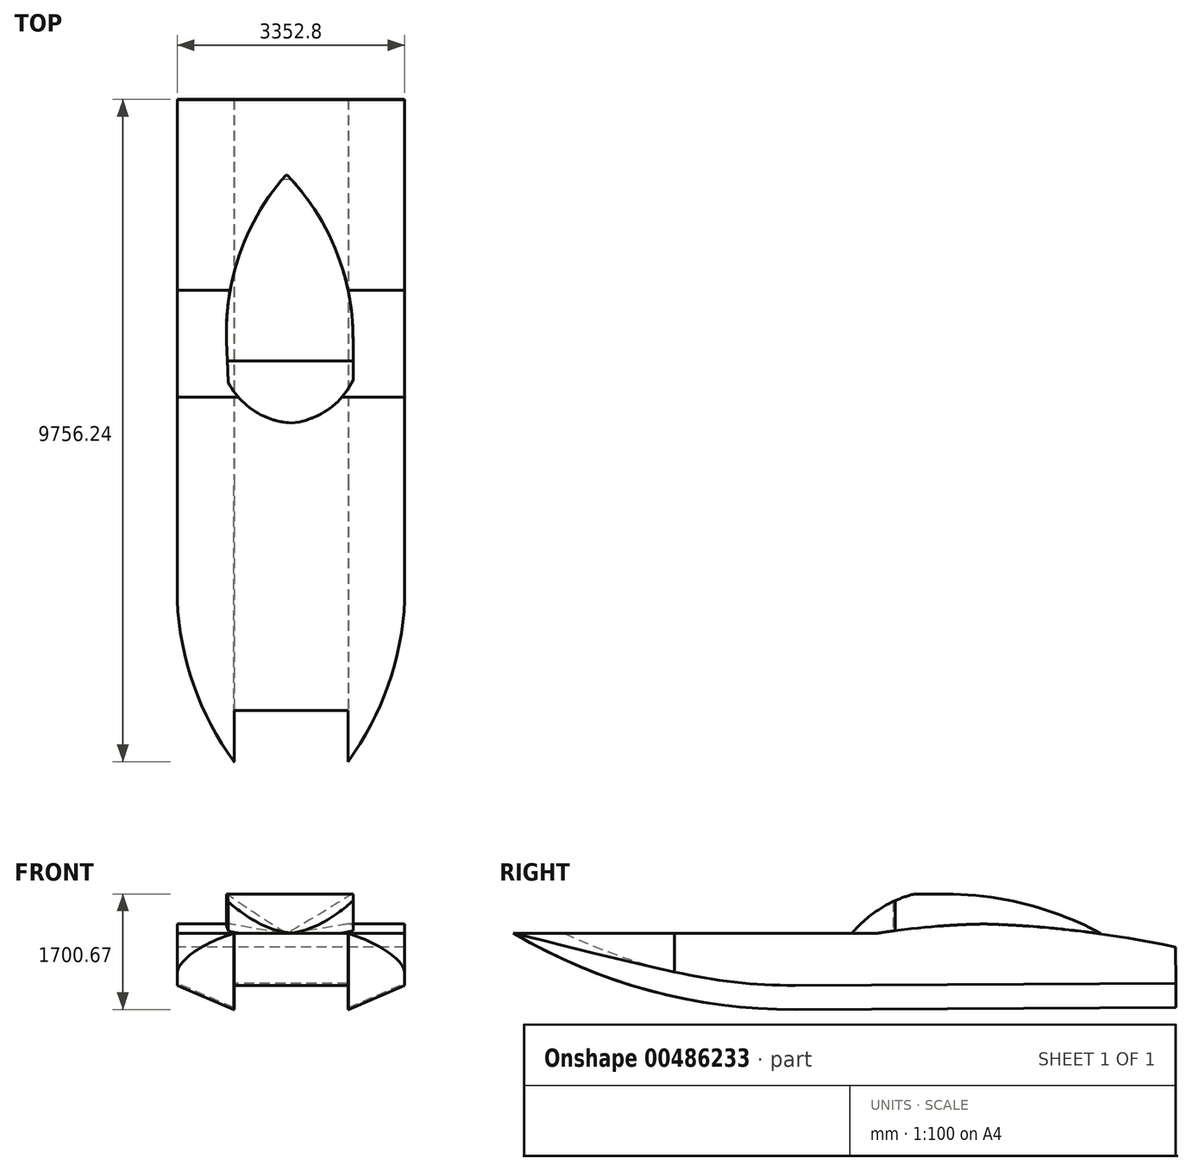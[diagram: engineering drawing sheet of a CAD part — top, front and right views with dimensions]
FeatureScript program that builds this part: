
annotation { "Feature Type Name" : "Feature", "Feature Type Description" : "" }
export const myFeature = defineFeature(function(context is Context, id is Id, definition is map)
    precondition{}
    {
        {
            var Q0;
            Q0=qCreatedBy(makeId("Right.planeOp"),FACE);
            var sketch = newSketch(context, id + "F0", { "sketchPlane" : qUnion([Q0])});
            skLineSegment(sketch, "E0", {"start": v(9903.4, 2819.64) * mm, "end": v(9906.18, 2286.25) * mm});
            skLineSegment(sketch, "E1", {"start": v(9906.18, 2286.25) * mm, "end": v(4296.5, 2257.1) * mm});
            skLineSegment(sketch, "E2", {"start": v(7101.34, 2271.67) * mm, "end": v(7096.72, 3160.66) * mm, "construction": true});
            skArc(sketch, "E3", {"start": v(9903.4, 2819.64) * mm, "mid": v(8507.76, 3053.5) * mm, "end": v(7096.72, 3160.66) * mm});
            skLineSegment(sketch, "E4", {"start": v(5524.18, 2263.47) * mm, "end": v(5520.22, 3025.46) * mm, "construction": true});
            skArc(sketch, "E5", {"start": v(7096.72, 3160.66) * mm, "mid": v(6306.11, 3120.55) * mm, "end": v(5520.22, 3025.46) * mm});
            skLineSegment(sketch, "E6", {"start": v(5520.22, 3025.46) * mm, "end": v(149.94, 3025.46) * mm});
            skArc(sketch, "E7", {"start": v(149.94, 3025.46) * mm, "mid": v(2186.92, 2445.37) * mm, "end": v(4296.5, 2257.1) * mm});
            skLineSegment(sketch, "E8", {"start": v(4296.5, 2257.1) * mm, "end": v(4298.35, 1901.5) * mm, "construction": true});
            skLineSegment(sketch, "E9", {"start": v(4298.35, 1901.5) * mm, "end": v(9906.18, 1930.65) * mm});
            skLineSegment(sketch, "E10", {"start": v(9906.18, 1930.65) * mm, "end": v(9906.18, 2286.25) * mm});
            skArc(sketch, "E11", {"start": v(149.94, 3025.46) * mm, "mid": v(2147.87, 2181.98) * mm, "end": v(4298.35, 1901.5) * mm});
            skSolve(sketch);
        }
        {
            var Q0;
            Q0=qSketchRegion(id+"F0",true);
            extrude(context, id + "F1", {"entities" : qUnion([Q0]), "depth" : 3352.8 * mm, "offsetDistance" : 25.4 * mm});
        }
        {
            var Q0;
            Q0=makeQuery(id+"F1.opExtrude","SWEPT_FACE",FACE,{"disambiguationData":[OSD([sQuery(id+"F0.wireOp",EDGE,"E6")])]});
            var sketch = newSketch(context, id + "F2", { "sketchPlane" : qUnion([Q0])});
            skLineSegment(sketch, "E12", {"start": v(1676.4, 5520.22) * mm, "end": v(1676.4, 5139.22) * mm, "construction": true});
            skLineSegment(sketch, "E13", {"start": v(1676.4, 5520.22) * mm, "end": v(2590.8, 5520.22) * mm, "construction": true});
            skLineSegment(sketch, "E14", {"start": v(2590.8, 5520.22) * mm, "end": v(1676.4, 5520.22) * mm, "construction": true});
            skLineSegment(sketch, "E15", {"start": v(1676.4, 5520.22) * mm, "end": v(762, 5520.22) * mm, "construction": true});
            skLineSegment(sketch, "E16", {"start": v(1612.43, 8801.7) * mm, "end": v(1676.4, 5520.22) * mm, "construction": true});
            skLineSegment(sketch, "E17", {"start": v(2590.8, 5520.22) * mm, "end": v(2590.8, 5774.22) * mm, "construction": true});
            skLineSegment(sketch, "E18", {"start": v(2590.8, 5774.22) * mm, "end": v(2590.8, 6383.82) * mm});
            skArc(sketch, "E19", {"start": v(1676.4, 5139.22) * mm, "mid": v(2218.54, 5334.4) * mm, "end": v(2590.8, 5774.22) * mm});
            skArc(sketch, "E20.MirrorCS", {"start": v(1691.25, 5139.5) * mm, "mid": v(1141.92, 5313.42) * mm, "end": v(752.8, 5738.38) * mm});
            skLineSegment(sketch, "E21.MirrorCS", {"start": v(752.8, 5738.38) * mm, "end": v(729.04, 6347.52) * mm});
            skArc(sketch, "E22", {"start": v(1612.43, 8801.7) * mm, "mid": v(931.87, 7660.59) * mm, "end": v(729.04, 6347.52) * mm});
            skArc(sketch, "E23", {"start": v(2590.8, 6383.82) * mm, "mid": v(2336.94, 7687.98) * mm, "end": v(1612.43, 8801.7) * mm});
            skLineSegment(sketch, "E24", {"start": v(2590.8, 6383.82) * mm, "end": v(2590.8, 5774.22) * mm});
            skSolve(sketch);
        }
        {
            var Q0;
            Q0=qSketchRegion(id+"F2",true);
            extrude(context, id + "F3", {"entities" : qUnion([Q0]), "operationType" : NewBodyOperationType.ADD, "depth" : 914.4 * mm, "offsetDistance" : 25.4 * mm});
        }
        {
            var Q0;
            Q0=makeQuery(id+"F1.opExtrude","CAP_FACE",FACE,{"disambiguationData":[OSD([sQuery(id+"F0.wireOp",EDGE,"E0"),sQuery(id+"F0.wireOp",EDGE,"E1"),sQuery(id+"F0.wireOp",EDGE,"E3"),sQuery(id+"F0.wireOp",EDGE,"E5"),sQuery(id+"F0.wireOp",EDGE,"E6"),sQuery(id+"F0.wireOp",EDGE,"E7")])],"isStart":false});
            var sketch = newSketch(context, id + "F4", { "sketchPlane" : qUnion([Q0])});
            skArc(sketch, "E25", {"start": v(6051.27, 3602.06) * mm, "mid": v(5549.4, 3384.98) * mm, "end": v(5137.42, 3025.46) * mm});
            skLineSegment(sketch, "E26", {"start": v(6051.27, 3602.06) * mm, "end": v(6508.47, 3602.06) * mm});
            skLineSegment(sketch, "E27", {"start": v(5137.42, 3025.46) * mm, "end": v(5137.42, 4052.91) * mm});
            skLineSegment(sketch, "E28", {"start": v(5137.42, 4052.91) * mm, "end": v(8976.57, 4052.91) * mm});
            skArc(sketch, "E29", {"start": v(8816.33, 3012.9) * mm, "mid": v(7699.4, 3452.45) * mm, "end": v(6508.47, 3602.06) * mm});
            skLineSegment(sketch, "E30", {"start": v(8816.33, 3012.9) * mm, "end": v(8976.57, 4052.91) * mm});
            skSolve(sketch);
        }
        {
            var Q0;
            Q0=qSketchRegion(id+"F4",true);
            extrude(context, id + "F5", {"entities" : qUnion([Q0]), "operationType" : NewBodyOperationType.REMOVE, "oppositeDirection" : true, "depth" : 3352.8 * mm, "offsetDistance" : 25.4 * mm});
        }
        {
            var Q0;
            Q0=makeQuery(id+"F1.opExtrude","SWEPT_FACE",FACE,{"disambiguationData":[OSD([sQuery(id+"F0.wireOp",EDGE,"E0")])]});
            var sketch = newSketch(context, id + "F6", { "sketchPlane" : qUnion([Q0])});
            skSolve(sketch);
        }
        {
            var Q0;
            Q0=makeQuery(id+"F1.opExtrude","SWEPT_FACE",FACE,{"disambiguationData":[OSD([sQuery(id+"F0.wireOp",EDGE,"E10")])]});
            var sketch = newSketch(context, id + "F7", { "sketchPlane" : qUnion([Q0])});
            skLineSegment(sketch, "E31", {"start": v(-1676.4, 2286.25) * mm, "end": v(0, 2286.25) * mm, "construction": true});
            skLineSegment(sketch, "E32", {"start": v(0, 2286.25) * mm, "end": v(-1676.4, 2286.25) * mm, "construction": true});
            skLineSegment(sketch, "E33", {"start": v(-1676.4, 2286.25) * mm, "end": v(-3352.8, 2286.25) * mm, "construction": true});
            skLineSegment(sketch, "E34", {"start": v(-1676.4, 2286.25) * mm, "end": v(-838.2, 2286.25) * mm, "construction": true});
            skLineSegment(sketch, "E35", {"start": v(-838.2, 2286.25) * mm, "end": v(-1676.4, 2286.25) * mm, "construction": true});
            skLineSegment(sketch, "E36", {"start": v(-1676.4, 2286.25) * mm, "end": v(-2514.6, 2286.25) * mm, "construction": true});
            skLineSegment(sketch, "E37", {"start": v(-2514.6, 2286.25) * mm, "end": v(-2514.6, 1930.65) * mm});
            skLineSegment(sketch, "E38", {"start": v(-838.2, 2286.25) * mm, "end": v(-838.2, 1930.65) * mm});
            skLineSegment(sketch, "E39", {"start": v(-3352.8, 1742.88) * mm, "end": v(-3352.8, 2286.25) * mm});
            skLineSegment(sketch, "E40", {"start": v(-2514.6, 1930.65) * mm, "end": v(-2514.6, 1742.88) * mm});
            skLineSegment(sketch, "E41", {"start": v(-2514.6, 1742.88) * mm, "end": v(-838.2, 1742.88) * mm});
            skLineSegment(sketch, "E42", {"start": v(-838.2, 1742.88) * mm, "end": v(-838.2, 1930.65) * mm});
            skLineSegment(sketch, "E43", {"start": v(0, 2286.25) * mm, "end": v(381.6, 2006.47) * mm});
            skLineSegment(sketch, "E44", {"start": v(-838.2, 1742.88) * mm, "end": v(192.5, 1742.88) * mm});
            skLineSegment(sketch, "E45", {"start": v(192.5, 1742.88) * mm, "end": v(381.6, 2006.47) * mm});
            skLineSegment(sketch, "E46", {"start": v(-3352.8, 1742.88) * mm, "end": v(-2514.6, 1742.88) * mm});
            skLineSegment(sketch, "E47", {"start": v(-838.2, 1930.65) * mm, "end": v(-831.85, 1930.65) * mm});
            skLineSegment(sketch, "E48", {"start": v(-831.85, 1930.65) * mm, "end": v(0, 2286.25) * mm});
            skLineSegment(sketch, "E49", {"start": v(-1676.4, 2286.25) * mm, "end": v(-1676.4, 1972.3) * mm, "construction": true});
            skLineSegment(sketch, "E50.MirrorCS", {"start": v(-2514.6, 1930.65) * mm, "end": v(-2520.95, 1930.65) * mm});
            skLineSegment(sketch, "E51.MirrorCS", {"start": v(-2520.95, 1930.65) * mm, "end": v(-3352.8, 2286.25) * mm});
            skSolve(sketch);
        }
        {
            var Q0;
            {var subQ0=sQuery(id+"F7.wireOp",EDGE,"E51.MirrorCS");Q0=makeQuery(id+"F7.imprint","IMPRINT",FACE,{"disambiguationData":[TD([[makeQuery(id+"F7.imprint","IMPRINT",EDGE,{"derivedFrom":subQ0}),1.0]])]});}
            var Q1;
            Q1=makeQuery(id+"F7.imprint","IMPRINT",FACE,{"disambiguationData":[TD([[makeQuery(id+"F7.imprint","IMPRINT",EDGE,{"derivedFrom":sQuery(id+"F7.wireOp",EDGE,"E40")}),-1.0]])]});
            var Q2;
            {var subQ0=sQuery(id+"F7.wireOp",EDGE,"E40");Q2=makeQuery(id+"F7.imprint","IMPRINT",FACE,{"disambiguationData":[TD([[makeQuery(id+"F7.imprint","IMPRINT",EDGE,{"derivedFrom":subQ0}),1.0]])]});}
            var Q3;
            Q3=makeQuery(id+"F7.imprint","IMPRINT",FACE,{"disambiguationData":[TD([[makeQuery(id+"F7.imprint","IMPRINT",EDGE,{"derivedFrom":sQuery(id+"F7.wireOp",EDGE,"E42")}),-1.0]])]});
            var Q4;
            {var subQ0=sQuery(id+"F7.wireOp",EDGE,"E48");Q4=makeQuery(id+"F7.imprint","IMPRINT",FACE,{"disambiguationData":[TD([[makeQuery(id+"F7.imprint","IMPRINT",EDGE,{"derivedFrom":subQ0}),-1.0]])]});}
            var Q5;
            {var subQ0=sQuery(id+"F7.wireOp",EDGE,"E37");Q5=makeQuery(id+"F7.imprint","IMPRINT",FACE,{"disambiguationData":[TD([[makeQuery(id+"F7.imprint","IMPRINT",EDGE,{"derivedFrom":subQ0}),1.0]])]});}
            var Q6;
            Q6=makeQuery(id+"F1.opExtrude","CAP_EDGE",EDGE,{"disambiguationData":[OSD([sQuery(id+"F0.wireOp",EDGE,"E9")])],"isStart":false});
            var Q7;
            Q7=makeQuery(id+"F1.opExtrude","CAP_EDGE",EDGE,{"disambiguationData":[OSD([sQuery(id+"F0.wireOp",EDGE,"E11")])],"isStart":false});
            sweep(context, id + "F8", {"operationType" : NewBodyOperationType.REMOVE, "profiles" : qUnion([Q0, Q1, Q2, Q3, Q4, Q5]), "path" : qUnion([Q6, Q7])});
        }
        {
            var Q0;
            Q0=makeQuery(id+"F1.opExtrude","SWEPT_FACE",FACE,{"disambiguationData":[OSD([sQuery(id+"F0.wireOp",EDGE,"E6")])]});
            var sketch = newSketch(context, id + "F9", { "sketchPlane" : qUnion([Q0])});
            skArc(sketch, "E52", {"start": v(0, 2933.73) * mm, "mid": v(180.65, 1470.04) * mm, "end": v(838.2, 149.94) * mm});
            skLineSegment(sketch, "E53", {"start": v(1676.4, 901.53) * mm, "end": v(1676.4, 2869.19) * mm, "construction": true});
            skArc(sketch, "E54.MirrorCS", {"start": v(3352.8, 2933.73) * mm, "mid": v(3172.15, 1470.04) * mm, "end": v(2514.6, 149.94) * mm});
            skLineSegment(sketch, "E55", {"start": v(0, 2933.73) * mm, "end": v(-833.76, 377.76) * mm, "construction": true});
            skLineSegment(sketch, "E56", {"start": v(-833.76, 377.76) * mm, "end": v(0, 2933.73) * mm});
            skLineSegment(sketch, "E57", {"start": v(-833.76, 377.76) * mm, "end": v(838.2, 149.94) * mm});
            skLineSegment(sketch, "E58", {"start": v(2520.95, 149.94) * mm, "end": v(4820.35, 149.94) * mm});
            skLineSegment(sketch, "E59", {"start": v(4820.35, 149.94) * mm, "end": v(3352.8, 2933.73) * mm});
            skSolve(sketch);
        }
        {
            var Q0;
            Q0=qSketchRegion(id+"F9",true);
            var Q1;
            Q1=makeQuery(id+"F9.imprint","IMPRINT",FACE,{"disambiguationData":[TD([[makeQuery(id+"F9.imprint","IMPRINT",EDGE,{"derivedFrom":sQuery(id+"F9.wireOp",EDGE,"E58")}),1.0]])]});
            var Q2;
            {var subQ1=sQuery(id+"F0.wireOp",EDGE,"E6");var subQ2=makeQuery(id+"F1.opExtrude","SWEPT_FACE",FACE,{"disambiguationData":[OSD([subQ1])]});var subQ4=sQuery(id+"F0.wireOp",EDGE,"E11");var subQ5=makeQuery(id+"F8.opSweep","SWEPT_FACE",FACE,{"disambiguationData":[OSD([subQ4,sQuery(id+"F7.wireOp",EDGE,"E51.MirrorCS")])]});var subQ7=subQ2;var subQ10=makeQuery(id+"F8.boolean.opBoolean","INTERSECT",EDGE,{"derivedFrom":[subQ7,subQ5]});Q2=makeQuery(id+"F9.imprint","IMPRINT",FACE,{"disambiguationData":[TD([[makeQuery(id+"F9.imprint","IMPRINT",EDGE,{"derivedFrom":subQ10}),1.0]])]});}
            extrude(context, id + "F10", {"entities" : qUnion([Q0, Q1, Q2]), "operationType" : NewBodyOperationType.REMOVE, "oppositeDirection" : true, "depth" : 1320.8 * mm, "offsetDistance" : 25.4 * mm});
        }
    });
